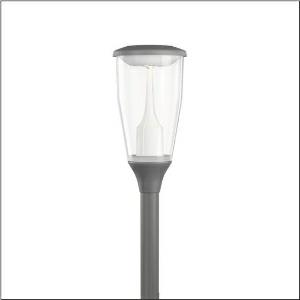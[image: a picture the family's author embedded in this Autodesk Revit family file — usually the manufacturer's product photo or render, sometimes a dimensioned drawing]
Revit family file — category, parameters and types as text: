
# Revit family: dl_11_iq___st1_2a_5xa5575ef14hp00022_53ae
name_source: partatom
category: Lighting Fixtures
units: mm (PartAtom-declared; Revit-internal decimal feet)

## family parameters
Cut with Voids When Loaded = No
Host = Face
Light Source = No
Part Type = Normal
Room Calculation Point = No
Round Connector Dimension = Use Diameter
Shared = No

## types (1)
- --- (1 x LED, 4840 lm, 33.6 W, 3000K)
    Apparent Load = 34 VA
    CIE Flux Codes = 23 60 93 95 100
    Color Rendering = 70
    Color Temperature = 3000K
    Default Elevation = 1800 mm
    Description = DL 11 iQ, mast luminaire, Module 540 iQ-SR, primary light control with 3 zone facetted reflector, of plastic, silver coated, highly specular, structured, primary optical cover: cover, of PMMA, transparent, light distribution: ST1.2a, light emission: direct distribution, primary light characteristic: asymmetric, installation type: post-top, LED, High Power LED, rated luminous flux: 4.840lm, luminous efficacy: 144lm/W, light colour: 730, colour temperature: 3000K, control gear: iQ Street-Remote, control: Street-Remote, Auto-Match, Temp-Guard, Lumen-Switch, Night-Set, Smart-Wire, Light-Fading, Desk-Remote (wireless, voltage-free reading and setting of iQ features in the workshop via application-optimized NFC function/RFID function), optimised constant luminous flux control (CLO 2.0), mains connection: 220..240V, AC, 50/60Hz, connection cable pre-assembled, cable length: 5,5m, start of lifetime: 34W, end of service life: 36W, reduction: 15W, luminaire housing, upper part, of diecast aluminium, coated, Siteco® metallic grey (DB 702S), spigot size: 76mm (post-top), mounting height: 3..5m, post-top mast mounting element, of diecast aluminium, coated, Siteco® metallic grey (DB 702S), Module 540 iQ-SR, traffic white (RAL 9016), equipment: Power, protection rating (complete): IP66, insulation class (complete): insulation class II (safety insulation), certification: CE, ENEC, ENEC+, VDE, impact resistance: IK07, packaging unit: 1 piece

Light Distribution: ST1.2a
    Height = 665 mm
    Lamp = 1 x LED
    Lamp Light Flux = 4840 lm
    Lamp Power = 33.6 W
    Lamp count = 1
    Length = 334 mm
    Luminous efficacy = 144 lm/W
    Manufacturer = Siteco
    ModVariant = No
    Model = 5XA5575EF14HP00022
    Number of Poles = 1
    OnlyDefault = Yes
    Power Factor = 1
    Product Name = DL 11 iQ | ST1.2a
    Product group = mast luminaire | pylon top
    ProductGroupID = 6100
    Protection Class = Protection class II
    Protection Degree = IP 66
    RLX_Detail_Level = 1
    RLX_Emergency_Light_Flux = 0 lm
    RLX_Emergency_Type = 0
    RLX_Emergency_Type_DB = No
    RlxData = <blob elided: 141937 chars, md5=7b8c43f5>
    Socket = socket
    Standby Power = 0 W
    System Light Flux = 4840 lm
    System Power = 34 W
    Type Comments = factory setting: luminous flux: 100 % | dim-lin: 254 | 695 mA
    Type Image = l_1258354.jpg
    URL = http://relux.com
    VarID = @adj_053557
    Voltage = 0 V
    Weight = 0.00 kg
    Width = 0 mm  [stored 0 ft]

note: [stored X ft] marks values corroborated as IEEE doubles in the binary element streams (Revit-internal decimal feet)

## geometry (parser evidence)
native form markers: Blend x4, Sweep x9
no freeform markers — native parametric forms only
